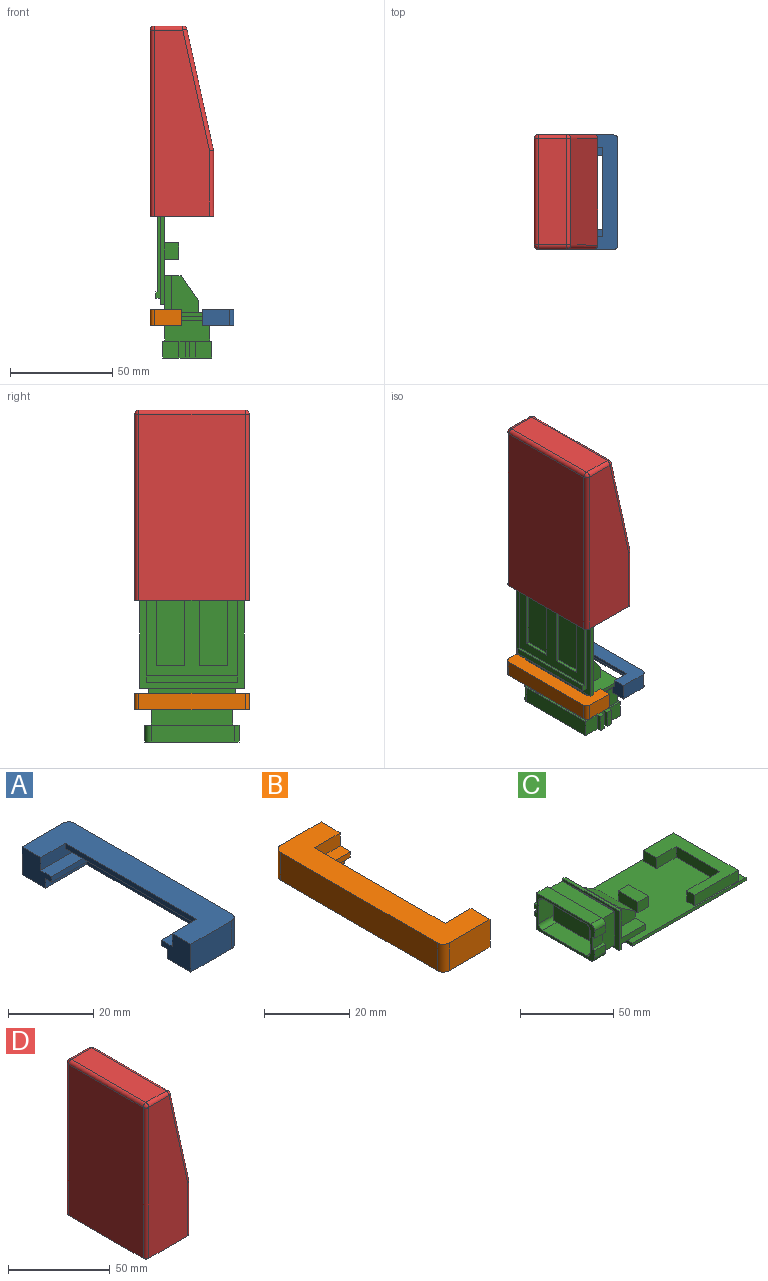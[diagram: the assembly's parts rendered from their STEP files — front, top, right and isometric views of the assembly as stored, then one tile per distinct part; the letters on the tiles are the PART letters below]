
ASSEMBLY  parts=4 mates=3
PART A: 22 faces, bbox 15.5x56x8 mm
  f0: plane 43.6x2.2mm, normal (-1,0,0), area 95.9mm2, adj f8,f11,f15,f21
  f1: plane 36.4x1.6mm, normal (-1,0,0), area 58.2mm2, adj f10,f11,f14,f20
  f2: plane 40.4x2.7mm, normal (-1,0,0), area 109.1mm2, adj f4,f10,f13,f19
  f3: plane 56x15.5mm, normal (0,0,1), area 508.8mm2, adj f5,f6,f7,f9,f12,f15,f16,f17
  f4: plane 56x15.5mm, normal (0,0,-1), area 312.8mm2, adj f2,f5,f6,f7,f12,f13,f16,f17
  f5: plane 52x8mm, normal (1,0,0), area 416mm2, adj f3,f4,f12,f18
  f6: plane 13.5x8mm, normal (0,-1,0), area 108mm2, adj f3,f4,f7,f12
  f7: plane 9.8x8mm, normal (-1,0,0), area 59.7mm2, adj f3,f4,f6,f10,f11,f13,f14,f15
  f8: plane 43.6x5.5mm, normal (0,0,-1), area 239.8mm2, adj f0,f9,f15,f21
  f9: plane 43.6x1.5mm, normal (-1,0,0), area 65.4mm2, adj f3,f8,f15,f21
  f10: plane 40.4x13.7mm, normal (0,0,-1), area 113mm2, adj f1,f2,f7,f13,f14,f17,f19,f20
  f11: plane 43.6x13.7mm, normal (0,0,1), area 156.9mm2, adj f0,f1,f7,f14,f15,f17,f20,f21
  f12: cylinder r=2mm len=8mm, axis (0,0,-1), area 25.1mm2, adj f3,f4,f5,f6
  f13: plane 13.7x2.7mm, normal (0,1,0), area 37mm2, adj f2,f4,f7,f10
  f14: plane 12.1x1.6mm, normal (0,1,0), area 19.4mm2, adj f1,f7,f10,f11
  f15: plane 13.7x3.7mm, normal (0,1,0), area 42.4mm2, adj f0,f3,f7,f8,f9,f11
  f16: plane 13.5x8mm, normal (0,1,0), area 108mm2, adj f3,f4,f17,f18
  f17: plane 9.8x8mm, normal (-1,0,0), area 59.7mm2, adj f3,f4,f10,f11,f16,f19,f20,f21
  f18: cylinder r=2mm len=8mm, axis (0,0,-1), area 25.1mm2, adj f3,f4,f5,f16
  f19: plane 13.7x2.7mm, normal (0,-1,0), area 37mm2, adj f2,f4,f10,f17
  f20: plane 12.1x1.6mm, normal (0,-1,0), area 19.4mm2, adj f1,f10,f11,f17
  f21: plane 13.7x3.7mm, normal (0,-1,0), area 42.4mm2, adj f0,f3,f8,f9,f11,f17
PART B: 22 faces, bbox 15.5x56x8 mm
  f0: plane 40.4x2.7mm, normal (1,0,0), area 109.1mm2, adj f2,f7,f14,f20
  f1: plane 43.4x12.5mm, normal (0,0,1), area 268mm2, adj f5,f10,f11,f13,f15,f17,f19,f21
  f2: plane 40.4x8.6mm, normal (0,0,-1), area 72.9mm2, adj f0,f10,f11,f13,f14,f17,f19,f20
  f3: plane 43.4x3.9mm, normal (0,0,-1), area 169.3mm2, adj f4,f5,f15,f21
  f4: plane 43.4x2mm, normal (1,0,0), area 86.8mm2, adj f3,f6,f15,f21
  f5: plane 43.4x1.7mm, normal (1,0,0), area 73.8mm2, adj f1,f3,f15,f21
  f6: plane 56x15.5mm, normal (0,0,1), area 493mm2, adj f4,f8,f9,f10,f12,f15,f16,f17
  f7: plane 56x15.5mm, normal (0,0,-1), area 518.8mm2, adj f0,f8,f9,f10,f12,f14,f16,f17
  f8: plane 13.5x8mm, normal (0,-1,0), area 108mm2, adj f6,f7,f10,f12
  f9: plane 52x8mm, normal (-1,0,0), area 416mm2, adj f6,f7,f12,f18
  f10: plane 9.7x8mm, normal (1,0,0), area 59.9mm2, adj f1,f2,f6,f7,f8,f13,f14,f15
  f11: plane 36.6x1.6mm, normal (1,0,0), area 58.6mm2, adj f1,f2,f13,f19
  f12: cylinder r=2mm len=8mm, axis (0,0,1), area 25.1mm2, adj f6,f7,f8,f9
  f13: plane 7.5x1.6mm, normal (0,1,0), area 12mm2, adj f1,f2,f10,f11
  f14: plane 8.6x2.7mm, normal (0,1,0), area 23.2mm2, adj f0,f2,f7,f10
  f15: plane 12.5x3.7mm, normal (0,1,0), area 38.5mm2, adj f1,f3,f4,f5,f6,f10
  f16: plane 13.5x8mm, normal (0,1,0), area 108mm2, adj f6,f7,f17,f18
  f17: plane 9.7x8mm, normal (1,0,0), area 59.9mm2, adj f1,f2,f6,f7,f16,f19,f20,f21
  f18: cylinder r=2mm len=8mm, axis (0,0,1), area 25.1mm2, adj f6,f7,f9,f16
  f19: plane 7.5x1.6mm, normal (0,-1,0), area 12mm2, adj f1,f2,f11,f17
  f20: plane 8.6x2.7mm, normal (0,-1,0), area 23.2mm2, adj f0,f2,f7,f17
  f21: plane 12.5x3.7mm, normal (0,-1,0), area 38.5mm2, adj f1,f3,f4,f5,f6,f17
PART C: 97 faces, bbox 112.3x51x27.4 mm
  f0: plane 5x1.5mm, normal (1,0,0), area 7.5mm2, adj f7,f87,f89,f94
  f1: plane 78x2.4mm, normal (0,1,0), area 119.7mm2, adj f85,f88,f89,f94,f95,f96
  f2: plane 70x1.5mm, normal (0,-1,0), area 105mm2, adj f3,f85,f89,f94
  f3: plane 14x1.5mm, normal (1,0,0), area 21mm2, adj f2,f4,f89,f94
  f4: plane 70x1.5mm, normal (0,1,0), area 105mm2, adj f3,f86,f89,f94
  f5: plane 70x1.5mm, normal (0,-1,0), area 105mm2, adj f6,f86,f89,f94
  f6: plane 14x1.5mm, normal (1,0,0), area 21mm2, adj f5,f7,f89,f94
  f7: plane 70x1.5mm, normal (0,1,0), area 105mm2, adj f0,f6,f89,f94
  f8: plane 86x2mm, normal (0,1,0), area 172mm2, adj f15,f16,f17,f89
  f9: plane 86x2mm, normal (0,-1,0), area 172mm2, adj f15,f16,f17,f89
  f10: plane 8.3x8mm, normal (0,-1,0), area 66.4mm2, adj f61,f62,f75,f77
  f11: plane 8.3x8mm, normal (0,1,0), area 66.4mm2, adj f55,f61,f62,f72
  f12: plane 8.3x2mm, normal (0,1,0), area 16.6mm2, adj f61,f62,f71,f73
  f13: plane 43x8mm, normal (1,0,0), area 272mm2, adj f15,f33,f36,f37,f39,f40,f41,f42
  f14: plane 43x18.5mm, normal (1,0,0), area 444.5mm2, adj f33,f34,f36,f37,f38,f40,f41,f42
  f15: plane 86x51mm, normal (0,0,1), area 2972mm2, adj f8,f9,f13,f16,f17,f18,f19,f20
  f16: plane 51x2mm, normal (-1,0,0), area 102mm2, adj f8,f9,f15,f32,f89
  f17: plane 51x2mm, normal (1,0,0), area 102mm2, adj f8,f9,f15,f89
  f18: plane 33x7mm, normal (-1,0,0), area 231mm2, adj f15,f19,f25,f26
  f19: plane 15x7mm, normal (0,-1,0), area 105mm2, adj f15,f18,f20,f26
  f20: plane 10x7mm, normal (-1,0,0), area 70mm2, adj f15,f19,f21,f26
  f21: plane 23x7mm, normal (0,1,0), area 161mm2, adj f15,f20,f22,f26
  f22: plane 49x7mm, normal (1,0,0), area 343mm2, adj f15,f21,f23,f26
  f23: plane 33x7mm, normal (0,-1,0), area 231mm2, adj f15,f22,f24,f26
  f24: plane 7x6mm, normal (-1,0,0), area 42mm2, adj f15,f23,f25,f26
  f25: plane 25x7mm, normal (0,1,0), area 175mm2, adj f15,f18,f24,f26
  f26: plane 49x33mm, normal (0,0,1), area 692mm2, adj f18,f19,f20,f21,f22,f23,f24,f25
  f27: plane 8x7mm, normal (0,1,0), area 56mm2, adj f15,f28,f30,f31
  f28: plane 15x7mm, normal (1,0,0), area 105mm2, adj f15,f27,f29,f31
  f29: plane 8x7mm, normal (0,-1,0), area 56mm2, adj f15,f28,f30,f31
  f30: plane 15x7mm, normal (-1,0,0), area 105mm2, adj f15,f27,f29,f31
  f31: plane 15x8mm, normal (0,0,1), area 120mm2, adj f27,f28,f29,f30
  f32: plane 43x4.8mm, normal (0,0,-1), area 206.4mm2, adj f16,f36,f37,f44
  f33: plane 18.25x8mm, normal (0,0,1), area 146mm2, adj f13,f14,f36,f40
  f34: plane 43x1.75mm, normal (0,0,1), area 75.3mm2, adj f14,f35,f36,f37
  f35: plane 43x26mm, normal (-1,0,0), area 437.4mm2, adj f34,f36,f37,f43,f45,f46,f47,f48
  f36: plane 26x20mm, normal (0,1,0), area 107.2mm2, adj f13,f14,f15,f32,f33,f34,f35,f43
  f37: plane 26x20mm, normal (0,-1,0), area 107.2mm2, adj f13,f14,f15,f32,f34,f35,f41,f43
  f38: plane 27x6mm, normal (0,0,1), area 162mm2, adj f14,f39,f40,f42
  f39: plane 27x12.25mm, normal (0.57,0,0.82), area 402.6mm2, adj f13,f38,f40,f42
  f40: plane 18.25x13mm, normal (0,1,0), area 185.2mm2, adj f13,f14,f33,f38,f39
  f41: plane 18.25x8mm, normal (0,0,1), area 146mm2, adj f13,f14,f37,f42
  f42: plane 18.25x13mm, normal (0,-1,0), area 185.2mm2, adj f13,f14,f38,f39,f41
  f43: plane 43x1.2mm, normal (0,0,-1), area 51.6mm2, adj f35,f36,f37,f44
  f44: plane 43x4mm, normal (1,0,0), area 172mm2, adj f32,f36,f37,f43
  f45: plane 32x2mm, normal (0,0,1), area 64mm2, adj f35,f53,f90,f93
  f46: plane 15x2mm, normal (0,1,0), area 30mm2, adj f35,f53,f90,f91
  f47: plane 32x2mm, normal (0,0,-1), area 64mm2, adj f35,f53,f91,f92
  f48: plane 15x2mm, normal (0,-1,0), area 30mm2, adj f35,f53,f92,f93
  f49: plane 40x10mm, normal (0,0,1), area 400mm2, adj f50,f52,f53,f62
  f50: plane 22x10mm, normal (0,1,0), area 220mm2, adj f49,f51,f53,f62
  f51: plane 40x10mm, normal (0,0,-1), area 400mm2, adj f50,f52,f53,f62
  f52: plane 22x10mm, normal (0,-1,0), area 220mm2, adj f49,f51,f53,f62
  f53: plane 40x22mm, normal (1,0,0), area 199.4mm2, adj f45,f46,f47,f48,f49,f50,f51,f52
  f54: plane 8.3x8mm, normal (0,1,0), area 66.4mm2, adj f60,f61,f62,f69
  f55: plane 41x8.3mm, normal (0,0,-1), area 340.3mm2, adj f11,f61,f62,f79
  f56: plane 33x11mm, normal (0,0,-1), area 363mm2, adj f61,f63,f81,f84
  f57: plane 15x11mm, normal (0,1,0), area 165mm2, adj f61,f63,f81,f82
  f58: plane 33x11mm, normal (0,0,1), area 363mm2, adj f61,f63,f82,f83
  f59: plane 15x11mm, normal (0,-1,0), area 165mm2, adj f61,f63,f83,f84
  f60: plane 41x8.3mm, normal (0,0,1), area 340.3mm2, adj f54,f61,f62,f80
  f61: plane 46x24mm, normal (-1,0,0), area 236.9mm2, adj f10,f11,f12,f54,f55,f56,f57,f58
  f62: plane 46x24mm, normal (1,0,0), area 168.1mm2, adj f10,f11,f12,f49,f50,f51,f52,f54
  f63: plane 39x21mm, normal (-1,0,0), area 541.3mm2, adj f56,f57,f58,f59,f65,f66,f67,f68
  f64: plane 27x10mm, normal (-1,0,0), area 270mm2, adj f65,f66,f67,f68
  f65: plane 10x5.7mm, normal (0,-1,0), area 57mm2, adj f63,f64,f66,f68
  f66: plane 27x5.7mm, normal (0,0,1), area 153.9mm2, adj f63,f64,f65,f67
  f67: plane 10x5.7mm, normal (0,1,0), area 57mm2, adj f63,f64,f66,f68
  f68: plane 27x5.7mm, normal (0,0,-1), area 153.9mm2, adj f63,f64,f65,f67
  f69: plane 8.3x2mm, normal (0,0,1), area 16.6mm2, adj f54,f61,f62,f70
  f70: plane 8.3x3mm, normal (0,1,0), area 24.9mm2, adj f61,f62,f69,f71
  f71: plane 8.3x2mm, normal (0,0,-1), area 16.6mm2, adj f12,f61,f62,f70
  f72: plane 8.3x2mm, normal (0,0,-1), area 16.6mm2, adj f11,f61,f62,f74
  f73: plane 8.3x2mm, normal (0,0,1), area 16.6mm2, adj f12,f61,f62,f74
  f74: plane 8.3x3mm, normal (0,1,0), area 24.9mm2, adj f61,f62,f72,f73
  f75: plane 8.3x2mm, normal (0,0,-1), area 16.6mm2, adj f10,f61,f62,f76
  f76: plane 8.3x5mm, normal (0,-1,0), area 41.5mm2, adj f61,f62,f75,f80
  f77: plane 8.3x2mm, normal (0,0,1), area 16.6mm2, adj f10,f61,f62,f78
  f78: plane 8.3x5mm, normal (0,-1,0), area 41.5mm2, adj f61,f62,f77,f79
  f79: cylinder r=3mm len=8.3mm, axis (-1,0,0), area 39.1mm2, adj f55,f61,f62,f78
  f80: cylinder r=3mm len=8.3mm, axis (-1,0,0), area 39.1mm2, adj f60,f61,f62,f76
  f81: cylinder r=3mm len=11mm, axis (-1,0,0), area 51.8mm2, adj f56,f57,f61,f63
  f82: cylinder r=3mm len=11mm, axis (1,0,0), area 51.8mm2, adj f57,f58,f61,f63
  f83: cylinder r=3mm len=11mm, axis (-1,0,0), area 51.8mm2, adj f58,f59,f61,f63
  f84: cylinder r=3mm len=11mm, axis (1,0,0), area 51.8mm2, adj f56,f59,f61,f63
  f85: plane 5x1.5mm, normal (1,0,0), area 7.5mm2, adj f1,f2,f89,f94
  f86: plane 7x1.5mm, normal (1,0,0), area 10.5mm2, adj f4,f5,f89,f94
  f87: plane 78x2.4mm, normal (0,-1,0), area 119.7mm2, adj f0,f88,f89,f94,f95,f96
  f88: plane 45x2.4mm, normal (-1,0,0), area 108mm2, adj f1,f87,f89,f95
  f89: plane 86x51mm, normal (0,0,-1), area 2836mm2, adj f0,f1,f2,f3,f4,f5,f6,f7
  f90: cylinder r=2mm len=2mm, axis (-1,0,0), area 6.3mm2, adj f35,f45,f46,f53
  f91: cylinder r=2mm len=2mm, axis (1,0,0), area 6.3mm2, adj f35,f46,f47,f53
  f92: cylinder r=2mm len=2mm, axis (-1,0,0), area 6.3mm2, adj f35,f47,f48,f53
  f93: cylinder r=2mm len=2mm, axis (1,0,0), area 6.3mm2, adj f35,f45,f48,f53
  f94: plane 75x45mm, normal (0,0,-1), area 1415mm2, adj f0,f1,f2,f3,f4,f5,f6,f7
  f95: plane 45x3mm, normal (0,0,-1), area 135mm2, adj f1,f87,f88,f96
  f96: plane 45x0.9mm, normal (1,0,0), area 40.5mm2, adj f1,f87,f94,f95
PART D: 41 faces, bbox 31x56x93 mm
  f0: plane 48x32mm, normal (-1,0,0), area 1536mm2, adj f5,f8,f15,f25
  f1: plane 52x32.22mm, normal (1,0,0), area 1675.3mm2, adj f2,f5,f27,f29
  f2: plane 59.21x52mm, normal (0.98,0,0.22), area 3152.9mm2, adj f1,f28,f31,f32
  f3: plane 52x14mm, normal (0,0,1), area 728mm2, adj f32,f33,f37,f38
  f4: plane 91x52mm, normal (-1,0,0), area 4732mm2, adj f5,f34,f38,f40
  f5: plane 56x31mm, normal (0,0,-1), area 332mm2, adj f0,f1,f4,f6,f9,f10,f11,f12
  f6: plane 89x48mm, normal (1,0,0), area 4272mm2, adj f5,f13,f16,f17
  f7: plane 48x10.39mm, normal (0,0,-1), area 498.8mm2, adj f17,f18,f22,f23
  f8: plane 57.43x48mm, normal (-0.98,0,-0.22), area 2822.8mm2, adj f0,f19,f23,f26
  f9: plane 91x27mm, normal (0,-1,0), area 2073.5mm2, adj f5,f27,f28,f33,f34
  f10: plane 89x23mm, normal (0,1,0), area 1686.3mm2, adj f5,f13,f15,f18,f19
  f11: plane 91x27mm, normal (0,1,0), area 2073.5mm2, adj f5,f29,f31,f37,f40
  f12: plane 89x23mm, normal (0,-1,0), area 1686.3mm2, adj f5,f16,f22,f25,f26
  f13: cylinder r=2mm len=89mm, axis (0,0,-1), area 279.6mm2, adj f5,f6,f10,f14
  f14: sphere r=2mm, area 6.3mm2, adj f13,f17,f18
  f15: cylinder r=2mm len=32mm, axis (0,0,1), area 100.3mm2, adj f0,f5,f10,f19
  f16: cylinder r=2mm len=89mm, axis (0,0,-1), area 279.6mm2, adj f5,f6,f12,f20
  f17: cylinder r=2mm len=48mm, axis (0,-1,0), area 150.8mm2, adj f6,f7,f14,f20
  f18: cylinder r=2mm len=10.39mm, axis (-1,0,0), area 32.6mm2, adj f7,f10,f14,f21
  f19: cylinder r=2mm len=57.86mm, axis (-0.22,0,0.98), area 184.5mm2, adj f8,f10,f15,f21
  f20: sphere r=2mm, area 6.3mm2, adj f16,f17,f22
  f21: sphere r=2mm, area 5.4mm2, adj f18,f19,f23
  f22: cylinder r=2mm len=10.39mm, axis (-1,0,0), area 32.6mm2, adj f7,f12,f20,f24
  f23: cylinder r=2mm len=48mm, axis (0,-1,0), area 130mm2, adj f7,f8,f21,f24
  f24: sphere r=2mm, area 5.4mm2, adj f22,f23,f26
  f25: cylinder r=2mm len=32mm, axis (0,0,1), area 100.3mm2, adj f0,f5,f12,f26
  f26: cylinder r=2mm len=57.86mm, axis (-0.22,0,0.98), area 184.5mm2, adj f8,f12,f24,f25
  f27: cylinder r=2mm len=32.22mm, axis (0,0,-1), area 101mm2, adj f1,f5,f9,f28
  f28: cylinder r=2mm len=59.64mm, axis (0.22,0,-0.98), area 190.2mm2, adj f2,f9,f27,f30
  f29: cylinder r=2mm len=32.22mm, axis (0,0,-1), area 101mm2, adj f1,f5,f11,f31
  f30: sphere r=2mm, area 5.4mm2, adj f28,f32,f33
  f31: cylinder r=2mm len=59.64mm, axis (0.22,0,-0.98), area 190.2mm2, adj f2,f11,f29,f35
  f32: cylinder r=2mm len=52mm, axis (0,1,0), area 140.8mm2, adj f2,f3,f30,f35
  f33: cylinder r=2mm len=14mm, axis (1,0,0), area 44mm2, adj f3,f9,f30,f36
  f34: cylinder r=2mm len=91mm, axis (0,0,1), area 285.9mm2, adj f4,f5,f9,f36
  f35: sphere r=2mm, area 5.4mm2, adj f31,f32,f37
  f36: sphere r=2mm, area 6.3mm2, adj f33,f34,f38
  f37: cylinder r=2mm len=14mm, axis (1,0,0), area 44mm2, adj f3,f11,f35,f39
  f38: cylinder r=2mm len=52mm, axis (0,1,0), area 163.4mm2, adj f3,f4,f36,f39
  f39: sphere r=2mm, area 6.3mm2, adj f37,f38,f40
  f40: cylinder r=2mm len=91mm, axis (0,0,1), area 285.9mm2, adj f4,f5,f11,f39
PLACE A t=(-66.17,1.76,-80.74)mm
PLACE B t=(-76.1,1.76,-80.74)mm
PLACE C rot(axis=(-0.71,0,-0.71),180deg) t=(-76,1.76,-35.19)mm
PLACE D t=(-76.1,1.76,-35.06)mm fixed
MATE slider A.f7 <-> B.f10  axis (-1,0,0) through (-52.67,-26.24,-84.74)mm
MATE slider C.f43 <-> B.f5  axis (-1,0,0) through (-75,-19.74,-83.59)mm
MATE slider D.f5 <-> B.f6  axis (0,0,-1) through (-78.1,1.76,-35.06)mm
